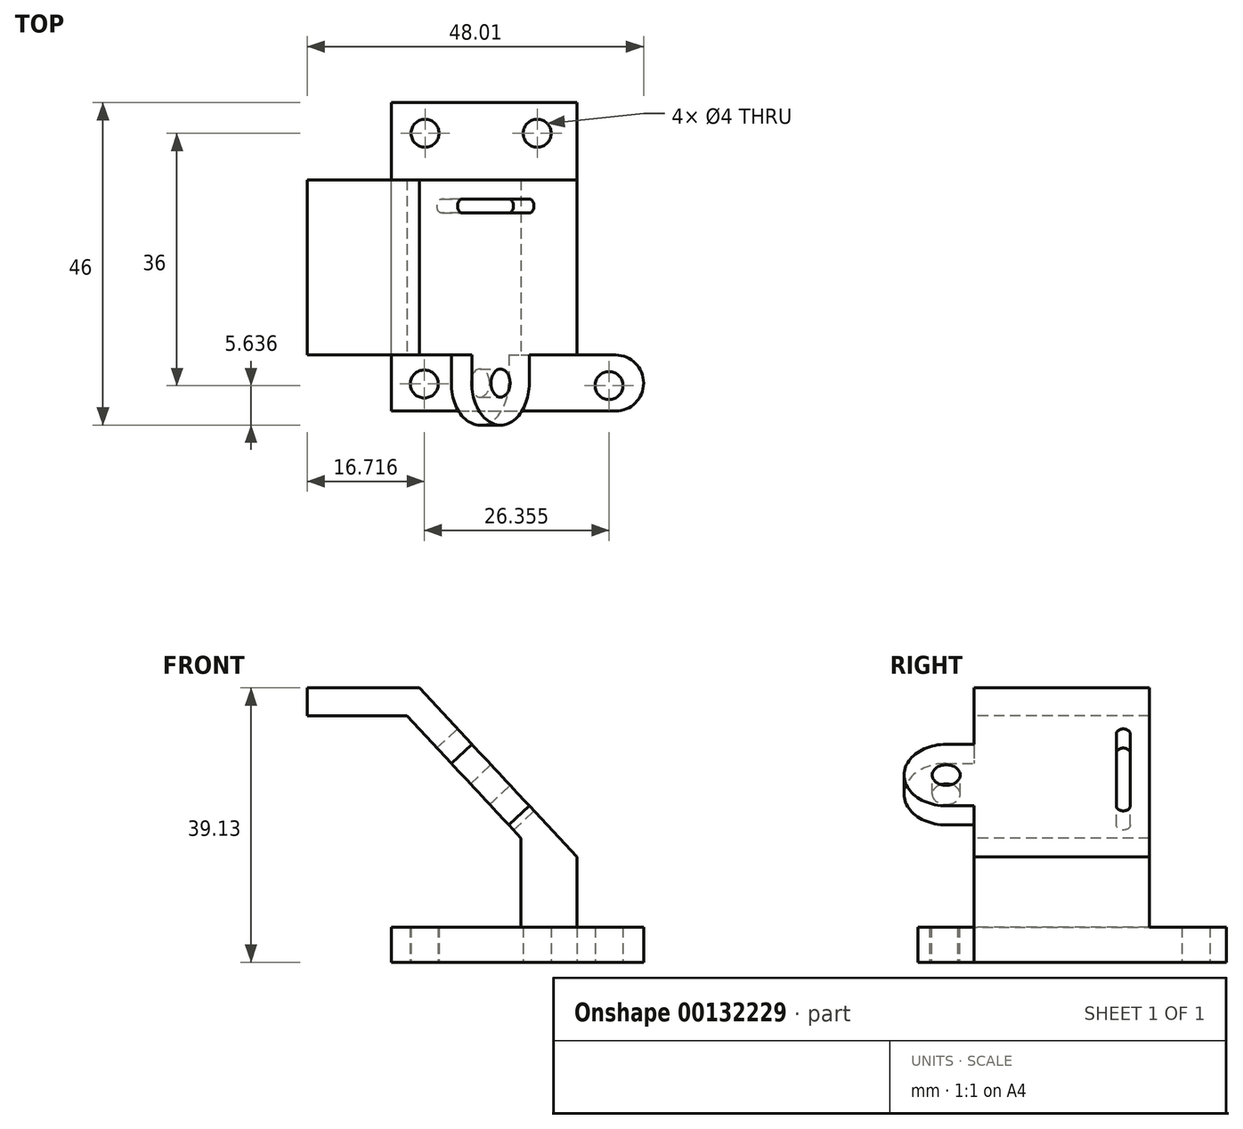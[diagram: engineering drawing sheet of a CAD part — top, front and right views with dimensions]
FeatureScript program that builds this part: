
annotation { "Feature Type Name" : "Feature", "Feature Type Description" : "" }
export const myFeature = defineFeature(function(context is Context, id is Id, definition is map)
    precondition{}
    {
        {
            var Q0;
            Q0=qCreatedBy(makeId("Top.planeOp"),FACE);
            var sketch = newSketch(context, id + "F0", { "sketchPlane" : qUnion([Q0])});
            skLineSegment(sketch, "E0", {"start": v(0, 0) * mm, "end": v(0, 44) * mm});
            skLineSegment(sketch, "E1", {"start": v(0, 44) * mm, "end": v(26.5, 44) * mm});
            skLineSegment(sketch, "E2", {"start": v(26.5, 44) * mm, "end": v(26.5, 8) * mm});
            skLineSegment(sketch, "E3", {"start": v(0, 0) * mm, "end": v(26.5, 0) * mm});
            skLineSegment(sketch, "E4", {"start": v(26.5, 8) * mm, "end": v(32, 8) * mm});
            skLineSegment(sketch, "E5", {"start": v(26.5, 0) * mm, "end": v(32, 0) * mm});
            skArc(sketch, "E6", {"start": v(32, 8) * mm, "mid": v(36, 4) * mm, "end": v(32, 0) * mm});
            skSolve(sketch);
        }
        {
            var Q0;
            Q0 = qSketchRegion(id + "F0", true);
            extrude(context, id + "F1", {"entities" : qUnion([Q0]), "depth" : 5 * mm});
        }
        {
            var Q0;
            Q0=makeQuery(id+"F1.opExtrude","SWEPT_FACE",FACE,{"disambiguationData":[OSD([sQuery(id+"F0.wireOp",EDGE,"E4")])]});
            var sketch = newSketch(context, id + "F2", { "sketchPlane" : qUnion([Q0])});
            skLineSegment(sketch, "E7", {"start": v(-26.5, 5) * mm, "end": v(-26.5, 15) * mm});
            skLineSegment(sketch, "E8", {"start": v(-26.5, 15) * mm, "end": v(-3.99, 39.13) * mm});
            skLineSegment(sketch, "E9", {"start": v(-3.99, 39.13) * mm, "end": v(12.01, 39.13) * mm});
            skLineSegment(sketch, "E10", {"start": v(12.01, 39.13) * mm, "end": v(12.01, 35.13) * mm});
            skLineSegment(sketch, "E11", {"start": v(12.01, 35.13) * mm, "end": v(-2.25, 35.13) * mm});
            skLineSegment(sketch, "E12", {"start": v(-2.25, 35.13) * mm, "end": v(-18.5, 17.71) * mm});
            skLineSegment(sketch, "E13", {"start": v(-18.5, 17.71) * mm, "end": v(-18.5, 5) * mm});
            skLineSegment(sketch, "E14", {"start": v(-18.5, 5) * mm, "end": v(-26.5, 5) * mm});
            skLineSegment(sketch, "E15", {"start": v(-18.5, 17.71) * mm, "end": v(-4.08, 17.71) * mm, "construction": true});
            skSolve(sketch);
        }
        {
            var Q0;
            Q0 = qSketchRegion(id + "F2", true);
            extrude(context, id + "F3", {"entities" : qUnion([Q0]), "operationType" : NewBodyOperationType.ADD, "depth" : 25 * mm});
        }
        {
            var Q0;
            Q0=makeQuery(id+"F3.opExtrude","SWEPT_FACE",FACE,{"disambiguationData":[OSD([sQuery(id+"F2.wireOp",EDGE,"E8")])]});
            cPlane(context, id + "F4", {"entities" : qUnion([Q0]), "cplaneType" : CPlaneType.OFFSET, "offset" : 0 * mm, "width" : 150 * mm, "height" : 150 * mm});
        }
        {
            var Q0;
            Q0=qCreatedBy(id+"F4.planeOp",FACE);
            var sketch = newSketch(context, id + "F5", { "sketchPlane" : qUnion([Q0])});
            skArc(sketch, "E16", {"start": v(4, 14.9) * mm, "mid": v(-2, 8.9) * mm, "end": v(4, 2.9) * mm});
            skLineSegment(sketch, "E17", {"start": v(4, 14.9) * mm, "end": v(8, 14.9) * mm});
            skLineSegment(sketch, "E18", {"start": v(8, 14.9) * mm, "end": v(8, 2.9) * mm});
            skLineSegment(sketch, "E19", {"start": v(8, 2.9) * mm, "end": v(4, 2.9) * mm});
            skCircle(sketch, "E20", {"center": v(4, 8.9) * mm, "radius": 2 * mm});
            skLineSegment(sketch, "E21.bottom", {"start": v(8, 14.9) * mm, "end": v(13.99, 14.9) * mm});
            skLineSegment(sketch, "E21.top", {"start": v(8, 2.95) * mm, "end": v(13.99, 2.95) * mm});
            skLineSegment(sketch, "E21.left", {"start": v(8, 14.9) * mm, "end": v(8, 2.95) * mm});
            skLineSegment(sketch, "E21.right", {"start": v(13.99, 14.9) * mm, "end": v(13.99, 2.95) * mm});
            skSolve(sketch);
        }
        {
            var Q0;
            Q0 = qSketchRegion(id + "F5", true);
            extrude(context, id + "F6", {"entities" : qUnion([Q0]), "operationType" : NewBodyOperationType.ADD, "oppositeDirection" : true, "depth" : 4 * mm});
        }
        {
            var Q0;
            Q0=qCreatedBy(id+"F4.planeOp",FACE);
            var sketch = newSketch(context, id + "F7", { "sketchPlane" : qUnion([Q0])});
            skLineSegment(sketch, "E22", {"start": v(29.27, 16.9) * mm, "end": v(29.27, 2.9) * mm, "construction": true});
            skArc(sketch, "E23.0.startCap", {"start": v(28.27, 16.9) * mm, "mid": v(29.27, 17.9) * mm, "end": v(30.27, 16.9) * mm});
            skArc(sketch, "E23.0.endCap", {"start": v(30.27, 2.9) * mm, "mid": v(29.27, 1.9) * mm, "end": v(28.27, 2.9) * mm});
            skLineSegment(sketch, "E23.0.left", {"start": v(30.27, 16.9) * mm, "end": v(30.27, 2.9) * mm});
            skLineSegment(sketch, "E23.0.right", {"start": v(28.27, 16.9) * mm, "end": v(28.27, 2.9) * mm});
            skSolve(sketch);
        }
        {
            var Q0;
            Q0 = qSketchRegion(id + "F7", true);
            extrude(context, id + "F8", {"entities" : qUnion([Q0]), "operationType" : NewBodyOperationType.REMOVE, "oppositeDirection" : true, "depth" : 10 * mm});
        }
        {
            var Q0;
            Q0=qCreatedBy(makeId("Top.planeOp"),FACE);
            var sketch = newSketch(context, id + "F9", { "sketchPlane" : qUnion([Q0])});
            skCircle(sketch, "E24", {"center": v(4.81, 39.64) * mm, "radius": 2 * mm});
            skCircle(sketch, "E25", {"center": v(20.81, 39.64) * mm, "radius": 2 * mm});
            skCircle(sketch, "E26", {"center": v(31.06, 3.64) * mm, "radius": 2 * mm});
            skCircle(sketch, "E27", {"center": v(4.7, 3.87) * mm, "radius": 2 * mm});
            skSolve(sketch);
        }
        {
            var Q0;
            Q0 = qSketchRegion(id + "F9", true);
            extrude(context, id + "F10", {"entities" : qUnion([Q0]), "operationType" : NewBodyOperationType.REMOVE, "depth" : 25 * mm});
        }
    });
